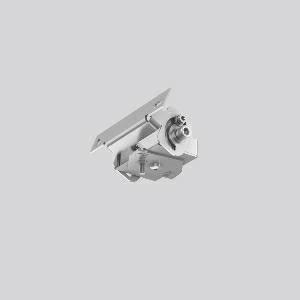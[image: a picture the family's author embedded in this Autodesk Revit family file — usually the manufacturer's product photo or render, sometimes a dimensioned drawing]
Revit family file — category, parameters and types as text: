
# Revit family: linedo_decke_wand_ausleger_982812_000_5280
name_source: partatom
category: Lighting Fixtures
units: mm (PartAtom-declared; Revit-internal decimal feet)

## family parameters
Cut with Voids When Loaded = No
Host = Face
Light Source = No
Part Type = Normal
Room Calculation Point = No
Round Connector Dimension = Use Diameter
Shared = No

## types (1)
- LINEDO Decke Wand Ausleger
    Apparent Load = 0 VA
    Default Elevation = 1800 mm
    Description = Ceiling/wall extension made of stainless steel. For 180°-pivotable horizontal installation of LINEDO luminaire modules, movable. 2 ceiling and wall brackets are required per luminaire module. With this accessory, the protection type of the luminaire module can be reduced to IP 20.
Colour: stainless steel
Length: 103 mm
Width: 47 mm
Height: 45 mm
Weight: 154 g
Type of Installation: Wall (surface)
    Height = 45 mm
    Lamp = 0 x
    Length = 103 mm
    Luminous efficacy = 0 lm/W
    Manufacturer = RZB
    ModVariant = No
    Model = 982812.000
    Mounting Place = Ceiling
    Mounting Type = Surface mounted
    Number of Poles = 1
    OnlyDefault = Yes
    Power Factor = 1
    Product Name = LINEDO Decke Wand Ausleger
    Product group = Surface mounted continuous line luminaire system
    ProductGroupID = 310
    Protection Class = Protection class
    Protection Degree = Degree of protection
    RLX_Detail_Level = 1
    RLX_Emergency_Light_Flux = 0 lm
    RLX_Emergency_Type = 0
    RLX_Emergency_Type_DB = No
    RlxData = <blob elided: 12625 chars, md5=ce7df821>
    Standby Power = 0 W
    System Light Flux = 0 lm
    System Power = 0 W
    Type Comments = Product without accessories
    Type Image = 982812.000.jpg
    URL = http://relux.com
    VarID = ---
    Voltage = 0 V
    Weight = 0.00 kg
    Width = 47 mm

## geometry (parser evidence)
native form markers: Sweep x9
no freeform markers — native parametric forms only
